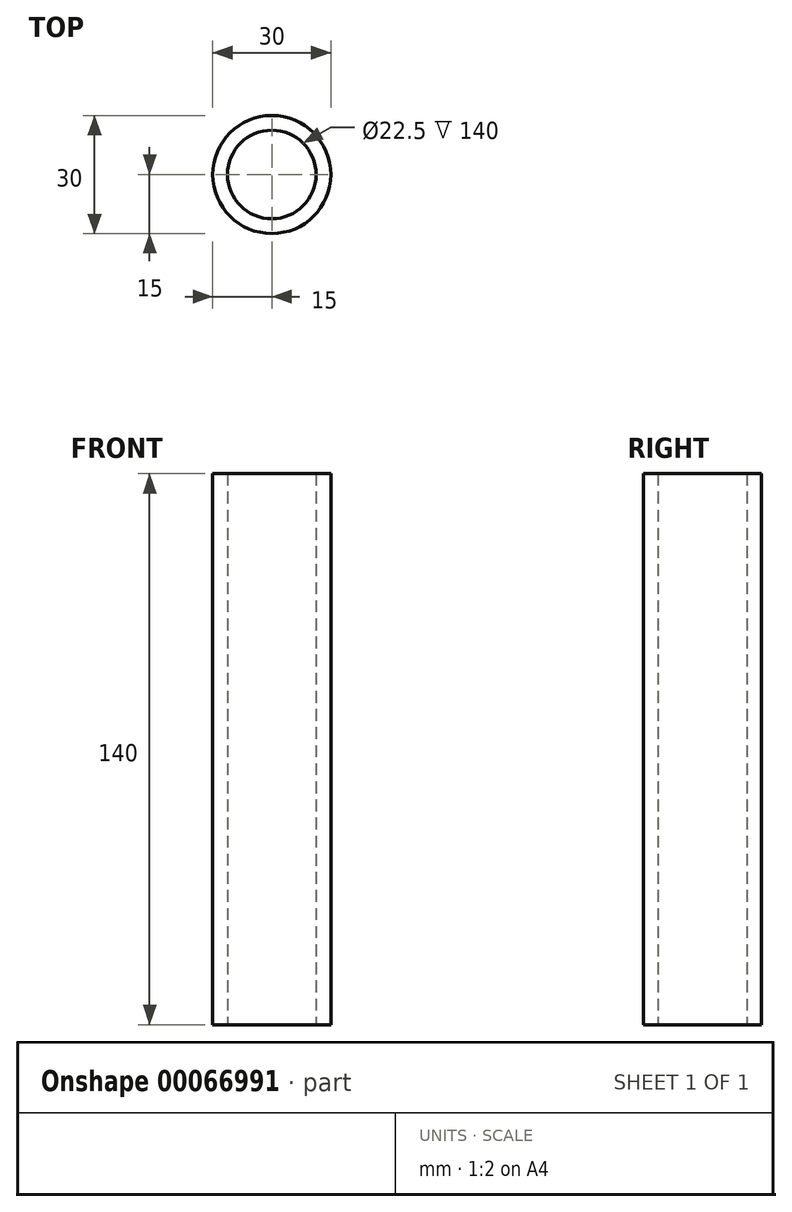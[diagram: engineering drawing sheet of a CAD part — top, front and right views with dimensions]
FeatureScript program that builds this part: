
annotation { "Feature Type Name" : "Feature", "Feature Type Description" : "" }
export const myFeature = defineFeature(function(context is Context, id is Id, definition is map)
    precondition{}
    {
        {
            var Q0;
            Q0=qCreatedBy(makeId("Top.planeOp"),FACE);
            var sketch = newSketch(context, id + "F0", { "sketchPlane" : qUnion([Q0])});
            skCircle(sketch, "E0", {"center": v(0, 0) * mm, "radius": 15 * mm});
            skCircle(sketch, "E1", {"center": v(0, 0) * mm, "radius": 11.25 * mm});
            skSolve(sketch);
        }
        {
            var Q0;
            Q0=makeQuery(id+"F0.imprint","IMPRINT",FACE,{"disambiguationData":[TD([[makeQuery(id+"F0.imprint","IMPRINT",EDGE,{"derivedFrom":sQuery(id+"F0.wireOp",EDGE,"E0")}),1.0]])]});
            extrude(context, id + "F1", {"entities" : qUnion([Q0]), "depth" : 140 * mm});
        }
    });
